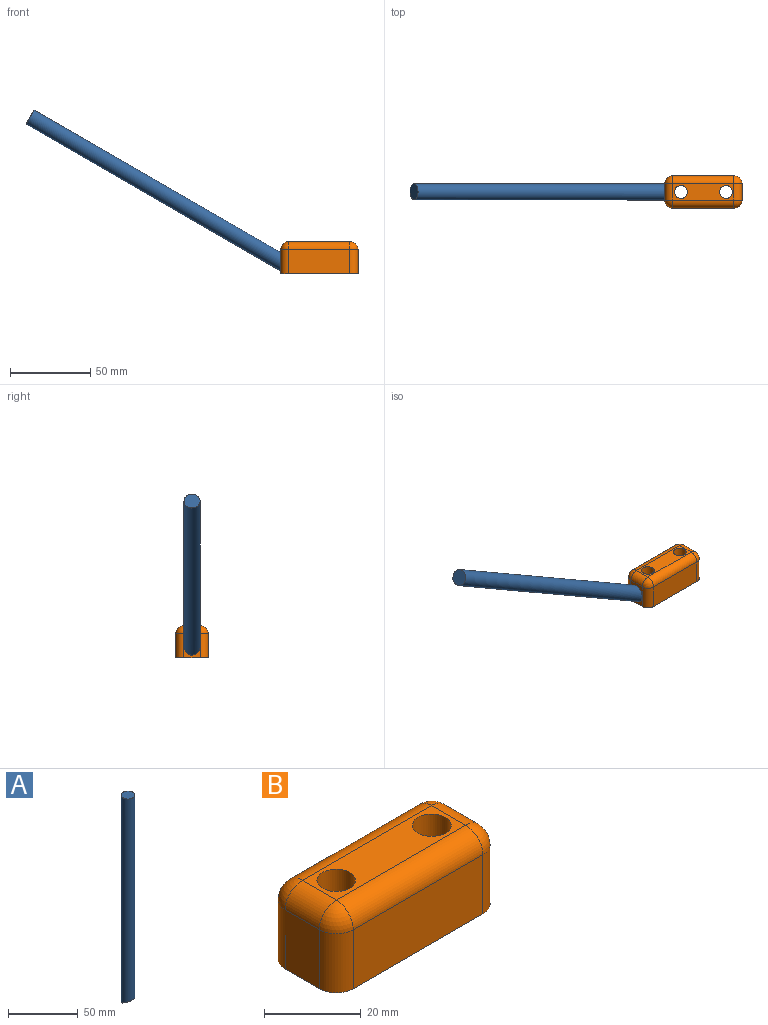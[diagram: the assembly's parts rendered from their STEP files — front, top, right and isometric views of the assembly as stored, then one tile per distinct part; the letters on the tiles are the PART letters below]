
ASSEMBLY  parts=2 mates=1
PART A: 3 faces, bbox 10x10x182.9 mm
  f0: cylinder r=5mm len=182.89mm, axis (0,0,-1), area 5654.9mm2, adj f1,f2
  f1: plane 10x10mm, normal (0,0,1), area 78.5mm2, adj f0
  f2: plane 10x10mm, normal (0,-0.5,-0.87), area 90.7mm2, adj f0
PART B: 20 faces, bbox 48x20x20 mm
  f0: plane 38x15mm, normal (0,1,0), area 570mm2, adj f7,f10,f16,f19
  f1: plane 15x10mm, normal (-1,0,0), area 150mm2, adj f7,f13,f17,f19
  f2: plane 38x15mm, normal (0,-1,0), area 570mm2, adj f7,f8,f12,f13
  f3: cylinder r=4mm len=20mm, axis (0,0,-1), area 502.7mm2, adj f6,f7
  f4: cylinder r=4mm len=20mm, axis (0,0,-1), area 502.7mm2, adj f6,f7
  f5: plane 15x10mm, normal (1,0,0), area 150mm2, adj f7,f8,f10,f11
  f6: plane 38x10mm, normal (0,0,1), area 279.5mm2, adj f3,f4,f11,f12,f16,f17
  f7: plane 48x20mm, normal (0,0,-1), area 838mm2, adj f0,f1,f2,f3,f4,f5,f8,f10
  f8: cylinder r=5mm len=15mm, axis (0,0,1), area 117.8mm2, adj f2,f5,f7,f9
  f9: sphere r=5mm, area 39.3mm2, adj f8,f11,f12
  f10: cylinder r=5mm len=15mm, axis (0,0,-1), area 117.8mm2, adj f0,f5,f7,f14
  f11: cylinder r=5mm len=10mm, axis (0,-1,0), area 78.5mm2, adj f5,f6,f9,f14
  f12: cylinder r=5mm len=38mm, axis (-1,0,0), area 298.5mm2, adj f2,f6,f9,f15
  f13: cylinder r=5mm len=15mm, axis (0,0,-1), area 117.8mm2, adj f1,f2,f7,f15
  f14: sphere r=5mm, area 39.3mm2, adj f10,f11,f16
  f15: sphere r=5mm, area 39.3mm2, adj f12,f13,f17
  f16: cylinder r=5mm len=38mm, axis (1,0,0), area 298.5mm2, adj f0,f6,f14,f18
  f17: cylinder r=5mm len=10mm, axis (0,1,0), area 78.5mm2, adj f1,f6,f15,f18
  f18: sphere r=5mm, area 39.3mm2, adj f16,f17,f19
  f19: cylinder r=5mm len=15mm, axis (0,0,1), area 117.8mm2, adj f0,f1,f7,f18
PLACE A rot(axis=(-0.45,-0.45,0.77),104.5deg) t=(-10,0,7.5)mm
PLACE B at identity fixed
MATE fastened A.f2 <-> B.f1  axis (1,0,0) through (-10,0,7.5)mm
